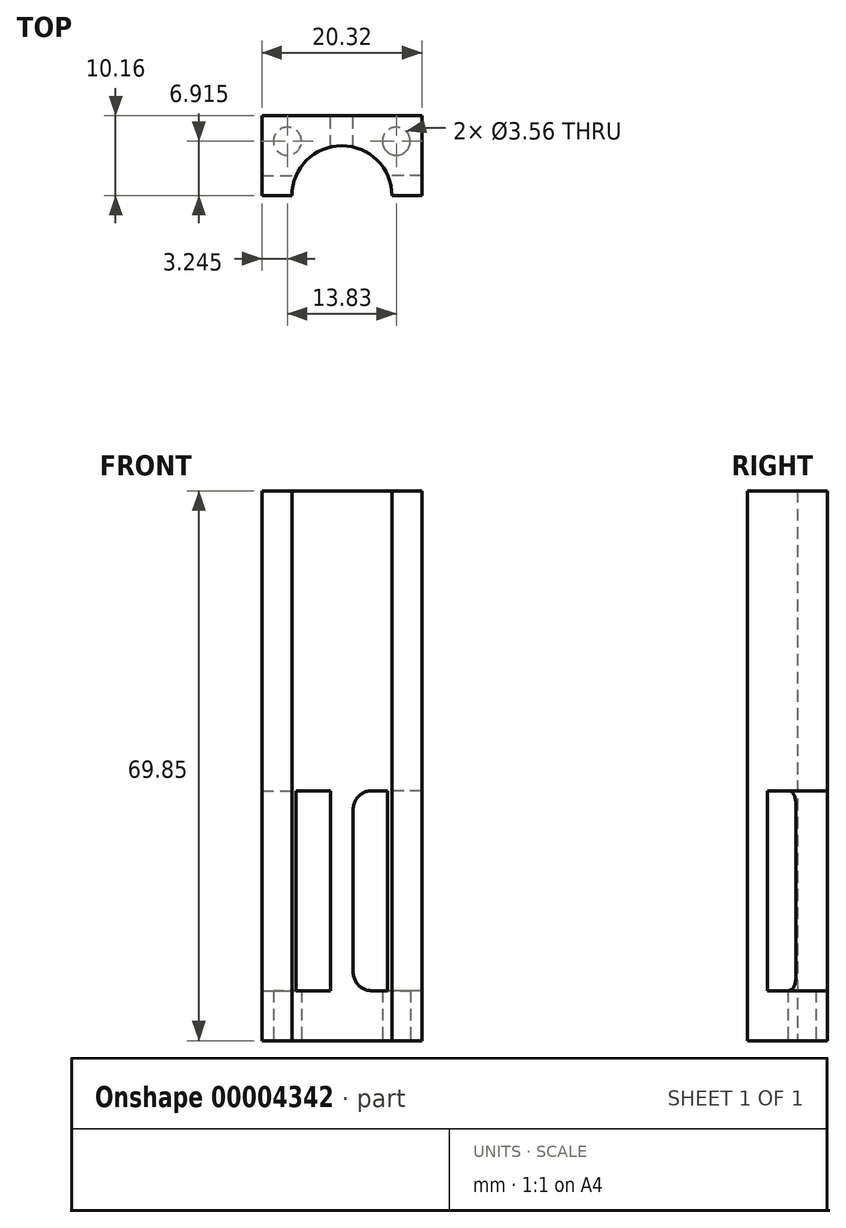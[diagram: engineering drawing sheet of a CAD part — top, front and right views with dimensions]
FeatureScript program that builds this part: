
annotation { "Feature Type Name" : "Feature", "Feature Type Description" : "" }
export const myFeature = defineFeature(function(context is Context, id is Id, definition is map)
    precondition{}
    {
        {
            var Q0;
            Q0=qCreatedBy(makeId("Top.planeOp"),FACE);
            var sketch = newSketch(context, id + "F0", { "sketchPlane" : qUnion([Q0])});
            skLineSegment(sketch, "E0.rect.bottom", {"start": v(6.91, -6.91) * mm, "end": v(-6.91, -6.91) * mm, "construction": true});
            skLineSegment(sketch, "E0.rect.top", {"start": v(6.91, 6.91) * mm, "end": v(-6.91, 6.91) * mm, "construction": true});
            skLineSegment(sketch, "E0.rect.left", {"start": v(6.91, -6.91) * mm, "end": v(6.91, 6.91) * mm, "construction": true});
            skLineSegment(sketch, "E0.rect.right", {"start": v(-6.91, -6.91) * mm, "end": v(-6.91, 6.91) * mm, "construction": true});
            skPoint(sketch, "E0.rect.middle", {"position": v(0, 0) * mm});
            skLineSegment(sketch, "E1", {"start": v(-6.91, -6.91) * mm, "end": v(6.91, 6.91) * mm, "construction": true});
            skCircle(sketch, "E2", {"center": v(6.91, 6.91) * mm, "radius": 1.78 * mm});
            skCircle(sketch, "E3", {"center": v(-6.91, 6.91) * mm, "radius": 1.78 * mm});
            skCircle(sketch, "E4", {"center": v(0, 0) * mm, "radius": 6.35 * mm});
            skLineSegment(sketch, "E5", {"start": v(-6.35, 0) * mm, "end": v(-10.16, 0) * mm});
            skLineSegment(sketch, "E6", {"start": v(-10.16, 0) * mm, "end": v(-10.16, 10.16) * mm});
            skLineSegment(sketch, "E7", {"start": v(-10.16, 10.16) * mm, "end": v(10.16, 10.16) * mm});
            skLineSegment(sketch, "E8", {"start": v(10.16, 10.16) * mm, "end": v(10.16, 0) * mm});
            skLineSegment(sketch, "E9", {"start": v(10.16, 0) * mm, "end": v(6.35, 0) * mm});
            skSolve(sketch);
        }
        {
            var Q0;
            Q0=makeQuery(id+"F0.imprint","IMPRINT",FACE,{"disambiguationData":[TD([[makeQuery(id+"F0.imprint","IMPRINT",EDGE,{"derivedFrom":sQuery(id+"F0.wireOp",EDGE,"E2")}),1.0]])]});
            var Q1;
            Q1=makeQuery(id+"F0.imprint","IMPRINT",FACE,{"disambiguationData":[TD([[makeQuery(id+"F0.imprint","IMPRINT",EDGE,{"derivedFrom":sQuery(id+"F0.wireOp",EDGE,"E2")}),-1.0]])]});
            var Q2;
            Q2=makeQuery(id+"F0.imprint","IMPRINT",FACE,{"disambiguationData":[TD([[makeQuery(id+"F0.imprint","IMPRINT",EDGE,{"derivedFrom":sQuery(id+"F0.wireOp",EDGE,"E3")}),1.0]])]});
            extrude(context, id + "F1", {"entities" : qUnion([Q0, Q1, Q2]), "depth" : 69.85 * mm});
        }
        {
            var Q0;
            Q0=makeQuery(id+"F0.imprint","IMPRINT",FACE,{"disambiguationData":[TD([[makeQuery(id+"F0.imprint","IMPRINT",EDGE,{"derivedFrom":sQuery(id+"F0.wireOp",EDGE,"E3")}),1.0]])]});
            var Q1;
            Q1=makeQuery(id+"F0.imprint","IMPRINT",FACE,{"disambiguationData":[TD([[makeQuery(id+"F0.imprint","IMPRINT",EDGE,{"derivedFrom":sQuery(id+"F0.wireOp",EDGE,"E2")}),1.0]])]});
            extrude(context, id + "F2", {"entities" : qUnion([Q0, Q1]), "operationType" : NewBodyOperationType.REMOVE, "depth" : 6.35 * mm});
        }
        {
            var Q0;
            Q0=makeQuery(id+"F1.opExtrude","SWEPT_FACE",FACE,{"disambiguationData":[OSD([sQuery(id+"F0.wireOp",EDGE,"E7")])]});
            var sketch = newSketch(context, id + "F3", { "sketchPlane" : qUnion([Q0])});
            skLineSegment(sketch, "E10.bottom", {"start": v(-10.16, 31.75) * mm, "end": v(-3.81, 31.75) * mm});
            skLineSegment(sketch, "E10.top", {"start": v(-10.16, 6.35) * mm, "end": v(-3.81, 6.35) * mm});
            skLineSegment(sketch, "E10.left", {"start": v(-10.16, 31.75) * mm, "end": v(-10.16, 6.35) * mm});
            skLineSegment(sketch, "E10.right", {"start": v(-1.43, 29.37) * mm, "end": v(-1.43, 8.73) * mm});
            skLineSegment(sketch, "E11", {"start": v(0, 20.73) * mm, "end": v(0, 0) * mm, "construction": true});
            skLineSegment(sketch, "E12.MirrorCS", {"start": v(10.16, 31.75) * mm, "end": v(1.43, 31.75) * mm});
            skLineSegment(sketch, "E13.MirrorCS", {"start": v(10.16, 31.75) * mm, "end": v(10.16, 6.35) * mm});
            skLineSegment(sketch, "E14.MirrorCS", {"start": v(1.43, 31.75) * mm, "end": v(1.43, 6.35) * mm});
            skLineSegment(sketch, "E15.MirrorCS", {"start": v(10.16, 6.35) * mm, "end": v(1.43, 6.35) * mm});
            skPoint(sketch, "E16.visualSharp", {"position": v(-1.43, 31.75) * mm});
            skArc(sketch, "E16.filletArc", {"start": v(-1.43, 29.37) * mm, "mid": v(-2.13, 31.05) * mm, "end": v(-3.81, 31.75) * mm});
            skPoint(sketch, "E17.visualSharp", {"position": v(-1.43, 6.35) * mm});
            skArc(sketch, "E17.filletArc", {"start": v(-3.81, 6.35) * mm, "mid": v(-2.13, 7.05) * mm, "end": v(-1.43, 8.73) * mm});
            skSolve(sketch);
        }
        {
            var Q0;
            Q0=makeQuery(id+"F3.imprint","IMPRINT",FACE,{"disambiguationData":[TD([[makeQuery(id+"F3.imprint","IMPRINT",EDGE,{"derivedFrom":sQuery(id+"F3.wireOp",EDGE,"E10.bottom")}),-1.0]])]});
            var Q1;
            Q1=makeQuery(id+"F3.imprint","IMPRINT",FACE,{"disambiguationData":[TD([[makeQuery(id+"F3.imprint","IMPRINT",EDGE,{"derivedFrom":sQuery(id+"F3.wireOp",EDGE,"E12.MirrorCS")}),1.0]])]});
            extrude(context, id + "F4", {"entities" : qUnion([Q0, Q1]), "operationType" : NewBodyOperationType.REMOVE, "oppositeDirection" : true, "depth" : 7.62 * mm});
        }
    });
